# Revit family: BE_24816_de_DE
name_source: partatom
category: Leuchten
revit_build: Autodesk Revit 2015 (Build: 20160512_0715(x64)
units: mm (PartAtom-declared; Revit-internal decimal feet)

## types (4) — shared parameters
AC/DC = AC/DC
Aktualisierung = 2017-08-09T04:09:38
BEGA_Dummy = Nein
BEGA_IES = Ja
BEGA_Intern = Ja
BEGA_Intern_Konstruktion = Ja
BEGA_Intern_an = Ja
BEGA_Intern_aus = Ja
Befestigungsbohrung = Ø 5,5 mm
Beschreibung = Flächenstrahler
Beschreibung_Sonderanfertigung = Hier können Sie Informationen zur Sonderanfertigung eintragen.
CE_Konformität = ja
Energieeffizienzklasse = LED A++ - A
Farbwiedergabeindex = Ra > 80
Frequenz = 0/50-60 Hz
Gewicht = 5.2 kg
Hersteller = BEGA
Lampe = LED 55.3 W
Lampenlichtstrom = 7620 lm
Lastklassifizierung = Beleuchtung
Lebensdauerkriterien = L70B50 @ 25 °C = 128000 h
Leuchtenlichtstrom = 6674 lm
Logo = BEGA_Logo.png
M_W = Nein
Material_02 = BEGA_Oberfläche_Silber_matt
Material_03 = BEGA_Oberfläche_Weiss_matt
Material_06 = BEGA_Oberfläche_Edelstahl_gebürstet
Material_09 = BEGA_Glas_klar
Material_11 = BEGA_Glas_opal
Material_15 = BEGA_Leuchtmedium_matt
Material_17 = BEGA_Reflektor
Produktdatenblatt = http://www.bega.de
Scheinlast = 0 VA
Schutzart = IP 65
Schutzklasse = I
Sonderanfertigung = Nein
Spannung = 240 V
Typenbild = 24816.png
URL = http://www.bega.de
Umgebungstemperatur = 25 °C
zero-valued in all types: BEGA_IES_X1, BEGA_IES_X2, BEGA_IES_Y1, BEGA_IES_Y2, BEGA_IES_Z1, BEGA_IES_Z2, Vorgabe-Ansicht

## per-type parameters (varying)
| type | BEGA_IES1 | BEGA_IES2 | Bestellnummer | Farbtemperatur | LED_Modulbezeichnung | M_A | M_G | Modell |
| BEGA_24816_Grafit_K4 | Nein | Ja | 24816 | 4000 K | LED-0773/840 | Nein | Ja | 24816 |
| BEGA_24816_Silber_K4 | Nein | Ja | 24816A | 4000 K | LED-0773/840 | Ja | Nein | 24816A |
| BEGA_24816_Silber_K3 | Ja | Nein | 24816AK3 | 3000 K | LED-0773/830 | Ja | Nein | 24816AK3 |
| BEGA_24816_Grafit_K3 | Ja | Nein | 24816K3 | 3000 K | LED-0773/830 | Nein | Ja | 24816K3 |

## geometry (parser evidence)
native form markers: Sweep x14
no freeform markers — native parametric forms only
